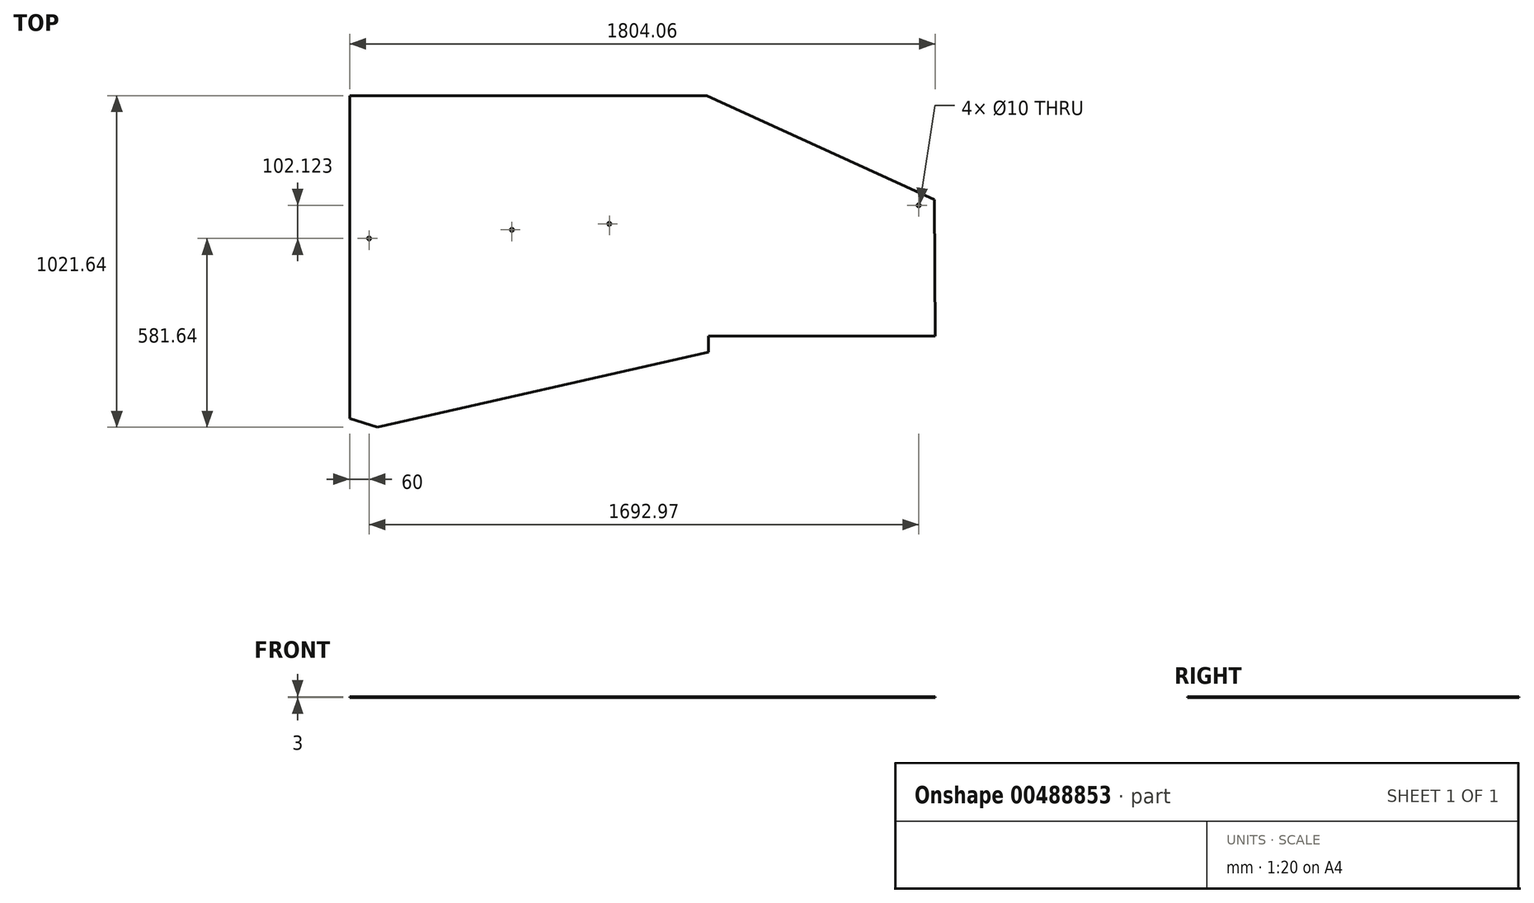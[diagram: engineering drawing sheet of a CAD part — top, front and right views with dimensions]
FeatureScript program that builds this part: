
annotation { "Feature Type Name" : "Feature", "Feature Type Description" : "" }
export const myFeature = defineFeature(function(context is Context, id is Id, definition is map)
    precondition{}
    {
        {
            var Q0;
            Q0=qCreatedBy(makeId("Top.planeOp"),FACE);
            var sketch = newSketch(context, id + "F0", { "sketchPlane" : qUnion([Q0])});
            skLineSegment(sketch, "E0", {"start": v(-1100, 0) * mm, "end": v(0, 0) * mm});
            skLineSegment(sketch, "E1", {"start": v(-1100, 0) * mm, "end": v(-1100, -995) * mm});
            skLineSegment(sketch, "E2", {"start": v(-1100, -995) * mm, "end": v(-1014.03, -1021.64) * mm});
            skLineSegment(sketch, "E3", {"start": v(-1014.03, -1021.64) * mm, "end": v(5.06, -790.38) * mm});
            skLineSegment(sketch, "E4", {"start": v(5.06, -790.38) * mm, "end": v(5.06, -740.38) * mm});
            skLineSegment(sketch, "E5", {"start": v(5.06, -740.38) * mm, "end": v(704.06, -740.38) * mm});
            skLineSegment(sketch, "E6", {"start": v(701.13, -320.72) * mm, "end": v(0, 0) * mm});
            skLineSegment(sketch, "E7", {"start": v(704.06, -740.38) * mm, "end": v(701.13, -320.72) * mm});
            skPoint(sketch, "E8.orphan", {"position": v(704.24, -322.14) * mm});
            skPoint(sketch, "E9.orphan", {"position": v(705.16, -740.38) * mm});
            skSolve(sketch);
        }
        {
            var Q0;
            Q0=makeQuery(id+"F0.imprint","IMPRINT",FACE,{"disambiguationData":[TD([[makeQuery(id+"F0.imprint","IMPRINT",EDGE,{"derivedFrom":sQuery(id+"F0.wireOp",EDGE,"E0")}),-1.0]])]});
            extrude(context, id + "F1", {"entities" : qUnion([Q0]), "depth" : 3 * mm});
        }
        {
            var Q0;
            Q0=makeQuery(id+"F1.opExtrude","CAP_FACE",FACE,{"disambiguationData":[OSD([sQuery(id+"F0.wireOp",EDGE,"E0"),sQuery(id+"F0.wireOp",EDGE,"E1"),sQuery(id+"F0.wireOp",EDGE,"E2"),sQuery(id+"F0.wireOp",EDGE,"E3"),sQuery(id+"F0.wireOp",EDGE,"E4"),sQuery(id+"F0.wireOp",EDGE,"E5"),sQuery(id+"F0.wireOp",EDGE,"MKm64Mz2-bf3f-YIpO-WHKg-M54kKkdSE8NB"),sQuery(id+"F0.wireOp",EDGE,"E6")])],"isStart":false});
            var sketch = newSketch(context, id + "F2", { "sketchPlane" : qUnion([Q0])});
            skCircle(sketch, "E10", {"center": v(652.97, -337.88) * mm, "radius": 5 * mm});
            skCircle(sketch, "E11", {"center": v(-600, -413.34) * mm, "radius": 5 * mm});
            skCircle(sketch, "E12", {"center": v(-300, -395.17) * mm, "radius": 5 * mm});
            skPoint(sketch, "E13.center.orphan", {"position": v(109.97, -294.93) * mm});
            skSolve(sketch);
        }
        {
            var Q0;
            Q0 = qSketchRegion(id + "F2", true);
            extrude(context, id + "F3", {"entities" : qUnion([Q0]), "operationType" : NewBodyOperationType.REMOVE, "oppositeDirection" : true, "depth" : 3 * mm, "offsetDistance" : 25 * mm});
        }
        {
            var Q0;
            Q0=makeQuery(id+"F1.opExtrude","CAP_FACE",FACE,{"disambiguationData":[OSD([sQuery(id+"F0.wireOp",EDGE,"E0"),sQuery(id+"F0.wireOp",EDGE,"E1"),sQuery(id+"F0.wireOp",EDGE,"E2"),sQuery(id+"F0.wireOp",EDGE,"E3"),sQuery(id+"F0.wireOp",EDGE,"E4"),sQuery(id+"F0.wireOp",EDGE,"E5"),sQuery(id+"F0.wireOp",EDGE,"MKm64Mz2-bf3f-YIpO-WHKg-M54kKkdSE8NB"),sQuery(id+"F0.wireOp",EDGE,"E6")])],"isStart":false});
            var sketch = newSketch(context, id + "F4", { "sketchPlane" : qUnion([Q0])});
            skCircle(sketch, "E14", {"center": v(-1040, -440) * mm, "radius": 5 * mm});
            skSolve(sketch);
        }
        {
            var Q0;
            Q0 = qSketchRegion(id + "F4", true);
            extrude(context, id + "F5", {"entities" : qUnion([Q0]), "operationType" : NewBodyOperationType.REMOVE, "oppositeDirection" : true, "depth" : 3 * mm, "offsetDistance" : 25 * mm});
        }
    });
